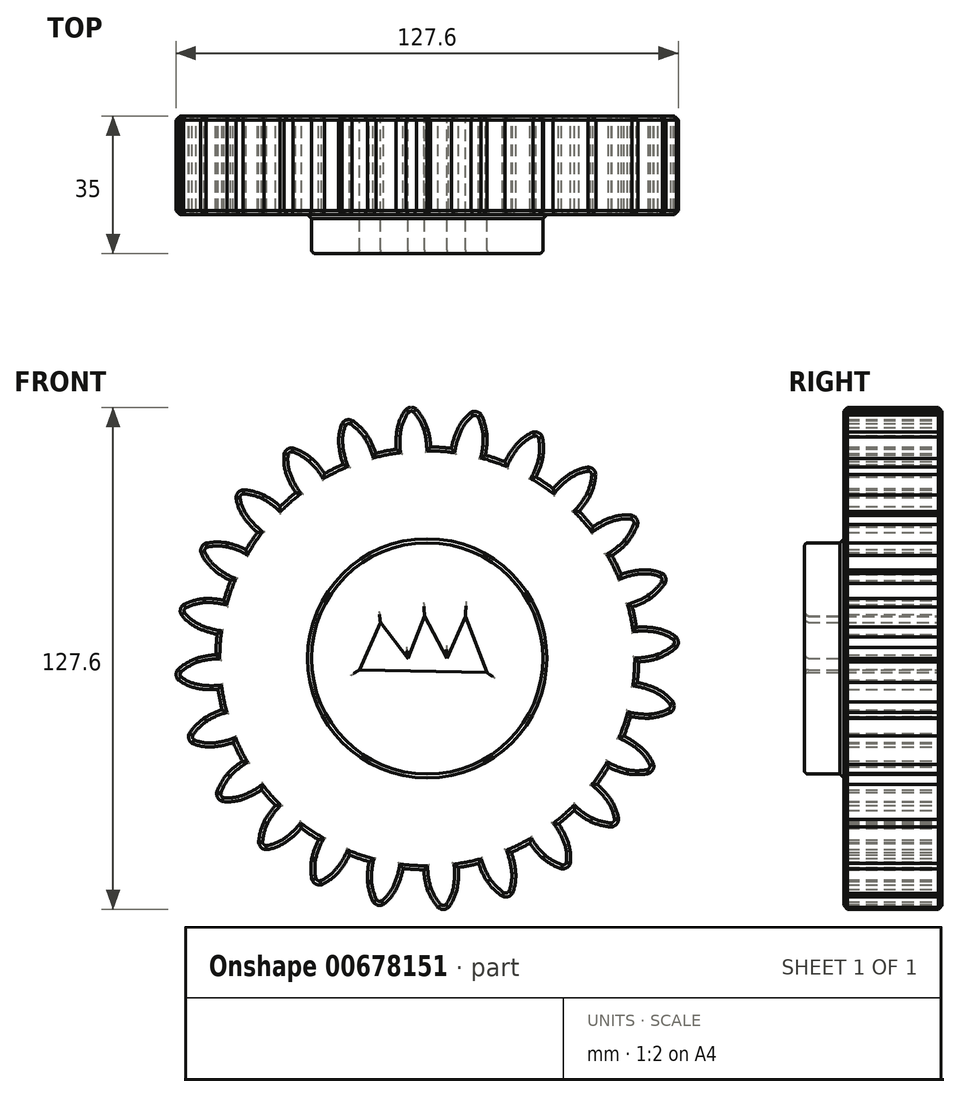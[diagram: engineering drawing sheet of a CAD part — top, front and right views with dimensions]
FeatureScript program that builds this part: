
annotation { "Feature Type Name" : "Feature", "Feature Type Description" : "" }
export const myFeature = defineFeature(function(context is Context, id is Id, definition is map)
    precondition{}
    {
        {
            var Q0;
            Q0=qCreatedBy(makeId("Front.planeOp"),FACE);
            var sketch = newSketch(context, id + "F0", { "sketchPlane" : qUnion([Q0])});
            skCircle(sketch, "E0", {"center": v(0, 0) * mm, "radius": 53.72 * mm});
            skCircle(sketch, "E1", {"center": v(0, 0) * mm, "radius": 58.67 * mm, "construction": true});
            skCircle(sketch, "E2", {"center": v(0, 0) * mm, "radius": 63.5 * mm, "construction": true});
            skLineSegment(sketch, "E3", {"start": v(0, 0) * mm, "end": v(0, 87.32) * mm, "construction": true});
            skLineSegment(sketch, "E4", {"start": v(0, 0) * mm, "end": v(-6.72, 102.52) * mm, "construction": true});
            skLineSegment(sketch, "E5", {"start": v(0, 58.67) * mm, "end": v(-57.61, 58.67) * mm, "construction": true});
            skLineSegment(sketch, "E6", {"start": v(0, 58.67) * mm, "end": v(-65.6, 34.8) * mm, "construction": true});
            skCircle(sketch, "E7", {"center": v(0, 0) * mm, "radius": 55.14 * mm, "construction": true});
            skCircle(sketch, "E8", {"center": v(0, 58.67) * mm, "radius": 14.6 * mm, "construction": true});
            skCircle(sketch, "E9", {"center": v(-13.72, 53.68) * mm, "radius": 14.6 * mm, "construction": true});
            skArc(sketch, "E10", {"start": v(0.88, 53.71) * mm, "mid": v(0.6, 56.22) * mm, "end": v(0, 58.67) * mm});
            skArc(sketch, "E11.MirrorCS", {"start": v(-7.66, 58.17) * mm, "mid": v(-6.86, 60.85) * mm, "end": v(-5.45, 63.27) * mm});
            skArc(sketch, "E12.MirrorCS", {"start": v(-7.88, 53.14) * mm, "mid": v(-7.93, 55.66) * mm, "end": v(-7.66, 58.17) * mm});
            skArc(sketch, "E13", {"start": v(0, 58.67) * mm, "mid": v(-1.18, 61.13) * mm, "end": v(-2.77, 63.34) * mm});
            skArc(sketch, "E14", {"start": v(-2.77, 63.34) * mm, "mid": v(-4.12, 63.8) * mm, "end": v(-5.45, 63.27) * mm});
            skCircle(sketch, "E15", {"center": v(0, 0) * mm, "radius": 29.38 * mm});
            skLineSegment(sketch, "E16", {"start": v(-17.22, -2.92) * mm, "end": v(-11.9, 9.15) * mm});
            skLineSegment(sketch, "E17", {"start": v(-11.9, 9.15) * mm, "end": v(-4.93, 0) * mm});
            skLineSegment(sketch, "E18", {"start": v(-4.93, 0) * mm, "end": v(-0.7, 10.8) * mm});
            skLineSegment(sketch, "E19", {"start": v(-0.7, 10.8) * mm, "end": v(5, 0) * mm});
            skLineSegment(sketch, "E20", {"start": v(5, 0) * mm, "end": v(9.74, 10.68) * mm});
            skLineSegment(sketch, "E21", {"start": v(9.74, 10.68) * mm, "end": v(15.18, -3.62) * mm});
            skLineSegment(sketch, "E22", {"start": v(15.18, -3.62) * mm, "end": v(-17.22, -2.92) * mm});
            skSolve(sketch);
        }
        {
            var Q0;
            {var subQ0=sQuery(id+"F0.wireOp",EDGE,"E0");var subQ1=makeQuery(id+"F0.imprint","INTERSECT",VERTEX,{"derivedFrom":[subQ0,sQuery(id+"F0.wireOp",EDGE,"E10")]});Q0=makeQuery(id+"F0.imprint","IMPRINT",FACE,{"disambiguationData":[TD([[makeQuery(id+"F0.imprint","IMPRINT",EDGE,{"disambiguationData":[TD([[subQ1,-1.0]])],"derivedFrom":subQ0}),1.0]])]});}
            var Q1;
            {var subQ1=sQuery(id+"F0.wireOp",EDGE,"E10");Q1=makeQuery(id+"F0.imprint","IMPRINT",FACE,{"disambiguationData":[TD([[makeQuery(id+"F0.imprint","IMPRINT",EDGE,{"derivedFrom":subQ1}),1.0]])]});}
            extrude(context, id + "F1", {"entities" : qUnion([Q0, Q1]), "depth" : 25 * mm, "offsetDistance" : 25 * mm});
        }
        {
            var Q0;
            Q0=makeQuery(id+"F1.opExtrude","SWEPT_BODY",BODY,{"disambiguationData":[OSD([sQuery(id+"F0.wireOp",EDGE,"E0"),sQuery(id+"F0.wireOp",EDGE,"E10"),sQuery(id+"F0.wireOp",EDGE,"E12.MirrorCS"),sQuery(id+"F0.wireOp",EDGE,"E11.MirrorCS"),sQuery(id+"F0.wireOp",EDGE,"E13"),sQuery(id+"F0.wireOp",EDGE,"E14")])]});
            var Q1;
            Q1=makeQuery(id+"F1.opExtrude","SWEPT_FACE",FACE,{"disambiguationData":[OSD([sQuery(id+"F0.wireOp",EDGE,"E0")])]});
            circularPattern(context, id + "F2", {"entities" : qUnion([Q0]), "axis" : qUnion([Q1]), "angle" : 360 * degree, "instanceCount" : 24, "equalSpace" : true});
        }
        {
            var Q0;
            Q0=makeQuery(id+"F0.imprint","IMPRINT",FACE,{"disambiguationData":[TD([[makeQuery(id+"F0.imprint","IMPRINT",EDGE,{"derivedFrom":sQuery(id+"F0.wireOp",EDGE,"E15")}),1.0]])]});
            extrude(context, id + "F3", {"entities" : qUnion([Q0]), "operationType" : NewBodyOperationType.ADD, "depth" : 35 * mm, "offsetDistance" : 25 * mm});
        }
        {
            var Q0;
            {var subQ0=makeQuery(id+"F1.opExtrude","CAP_FACE",FACE,{"disambiguationData":[OSD([sQuery(id+"F0.wireOp",EDGE,"E0"),sQuery(id+"F0.wireOp",EDGE,"E10"),sQuery(id+"F0.wireOp",EDGE,"E12.MirrorCS"),sQuery(id+"F0.wireOp",EDGE,"E11.MirrorCS"),sQuery(id+"F0.wireOp",EDGE,"E13"),sQuery(id+"F0.wireOp",EDGE,"E14"),sQuery(id+"F0.wireOp",EDGE,"E15")])],"isStart":false});Q0=makeQuery(id+"F3.boolean.opBoolean","MERGE",FACE,{"derivedFrom":[subQ0,makeQuery(id+"F2.opPattern","COPY",FACE,{"derivedFrom":subQ0,"instanceName":"1"}),makeQuery(id+"F2.opPattern","COPY",FACE,{"derivedFrom":subQ0,"instanceName":"2"}),makeQuery(id+"F2.opPattern","COPY",FACE,{"derivedFrom":subQ0,"instanceName":"3"}),makeQuery(id+"F2.opPattern","COPY",FACE,{"derivedFrom":subQ0,"instanceName":"4"}),makeQuery(id+"F2.opPattern","COPY",FACE,{"derivedFrom":subQ0,"instanceName":"5"}),makeQuery(id+"F2.opPattern","COPY",FACE,{"derivedFrom":subQ0,"instanceName":"6"}),makeQuery(id+"F2.opPattern","COPY",FACE,{"derivedFrom":subQ0,"instanceName":"7"}),makeQuery(id+"F2.opPattern","COPY",FACE,{"derivedFrom":subQ0,"instanceName":"8"}),makeQuery(id+"F2.opPattern","COPY",FACE,{"derivedFrom":subQ0,"instanceName":"9"}),makeQuery(id+"F2.opPattern","COPY",FACE,{"derivedFrom":subQ0,"instanceName":"10"}),makeQuery(id+"F2.opPattern","COPY",FACE,{"derivedFrom":subQ0,"instanceName":"11"}),makeQuery(id+"F2.opPattern","COPY",FACE,{"derivedFrom":subQ0,"instanceName":"12"}),makeQuery(id+"F2.opPattern","COPY",FACE,{"derivedFrom":subQ0,"instanceName":"13"}),makeQuery(id+"F2.opPattern","COPY",FACE,{"derivedFrom":subQ0,"instanceName":"14"}),makeQuery(id+"F2.opPattern","COPY",FACE,{"derivedFrom":subQ0,"instanceName":"15"}),makeQuery(id+"F2.opPattern","COPY",FACE,{"derivedFrom":subQ0,"instanceName":"16"}),makeQuery(id+"F2.opPattern","COPY",FACE,{"derivedFrom":subQ0,"instanceName":"17"}),makeQuery(id+"F2.opPattern","COPY",FACE,{"derivedFrom":subQ0,"instanceName":"18"}),makeQuery(id+"F2.opPattern","COPY",FACE,{"derivedFrom":subQ0,"instanceName":"19"}),makeQuery(id+"F2.opPattern","COPY",FACE,{"derivedFrom":subQ0,"instanceName":"20"}),makeQuery(id+"F2.opPattern","COPY",FACE,{"derivedFrom":subQ0,"instanceName":"21"}),makeQuery(id+"F2.opPattern","COPY",FACE,{"derivedFrom":subQ0,"instanceName":"22"}),makeQuery(id+"F2.opPattern","COPY",FACE,{"derivedFrom":subQ0,"instanceName":"23"})]});}
            chamfer(context, id + "F4", {"entities" : qUnion([Q0]), "width" : 1 * mm, "tangentPropagation" : true});
        }
        {
            var Q0;
            {var subQ0=sQuery(id+"F0.wireOp",EDGE,"E15");var subQ1=makeQuery(id+"F1.opExtrude","CAP_FACE",FACE,{"disambiguationData":[OSD([sQuery(id+"F0.wireOp",EDGE,"E0"),sQuery(id+"F0.wireOp",EDGE,"E10"),sQuery(id+"F0.wireOp",EDGE,"E12.MirrorCS"),sQuery(id+"F0.wireOp",EDGE,"E11.MirrorCS"),sQuery(id+"F0.wireOp",EDGE,"E13"),sQuery(id+"F0.wireOp",EDGE,"E14"),subQ0])],"isStart":true});Q0=makeQuery(id+"F3.boolean.opBoolean","MERGE",FACE,{"derivedFrom":[subQ1,makeQuery(id+"F2.opPattern","COPY",FACE,{"derivedFrom":subQ1,"instanceName":"1"}),makeQuery(id+"F2.opPattern","COPY",FACE,{"derivedFrom":subQ1,"instanceName":"2"}),makeQuery(id+"F2.opPattern","COPY",FACE,{"derivedFrom":subQ1,"instanceName":"3"}),makeQuery(id+"F2.opPattern","COPY",FACE,{"derivedFrom":subQ1,"instanceName":"4"}),makeQuery(id+"F2.opPattern","COPY",FACE,{"derivedFrom":subQ1,"instanceName":"5"}),makeQuery(id+"F2.opPattern","COPY",FACE,{"derivedFrom":subQ1,"instanceName":"6"}),makeQuery(id+"F2.opPattern","COPY",FACE,{"derivedFrom":subQ1,"instanceName":"7"}),makeQuery(id+"F2.opPattern","COPY",FACE,{"derivedFrom":subQ1,"instanceName":"8"}),makeQuery(id+"F2.opPattern","COPY",FACE,{"derivedFrom":subQ1,"instanceName":"9"}),makeQuery(id+"F2.opPattern","COPY",FACE,{"derivedFrom":subQ1,"instanceName":"10"}),makeQuery(id+"F2.opPattern","COPY",FACE,{"derivedFrom":subQ1,"instanceName":"11"}),makeQuery(id+"F2.opPattern","COPY",FACE,{"derivedFrom":subQ1,"instanceName":"12"}),makeQuery(id+"F2.opPattern","COPY",FACE,{"derivedFrom":subQ1,"instanceName":"13"}),makeQuery(id+"F2.opPattern","COPY",FACE,{"derivedFrom":subQ1,"instanceName":"14"}),makeQuery(id+"F2.opPattern","COPY",FACE,{"derivedFrom":subQ1,"instanceName":"15"}),makeQuery(id+"F2.opPattern","COPY",FACE,{"derivedFrom":subQ1,"instanceName":"16"}),makeQuery(id+"F2.opPattern","COPY",FACE,{"derivedFrom":subQ1,"instanceName":"17"}),makeQuery(id+"F2.opPattern","COPY",FACE,{"derivedFrom":subQ1,"instanceName":"18"}),makeQuery(id+"F2.opPattern","COPY",FACE,{"derivedFrom":subQ1,"instanceName":"19"}),makeQuery(id+"F2.opPattern","COPY",FACE,{"derivedFrom":subQ1,"instanceName":"20"}),makeQuery(id+"F2.opPattern","COPY",FACE,{"derivedFrom":subQ1,"instanceName":"21"}),makeQuery(id+"F2.opPattern","COPY",FACE,{"derivedFrom":subQ1,"instanceName":"22"}),makeQuery(id+"F2.opPattern","COPY",FACE,{"derivedFrom":subQ1,"instanceName":"23"}),makeQuery(id+"F3.opExtrude","CAP_FACE",FACE,{"disambiguationData":[OSD([subQ0,sQuery(id+"F0.wireOp",EDGE,"JNtdXsKn-sl94-sJaL-X6j9-ipqJ5UrsfOhM"),sQuery(id+"F0.wireOp",EDGE,"nhLlYziE-T9go-qMXb-Lngr-M2SgK2O0rp0T"),sQuery(id+"F0.wireOp",EDGE,"FmWoKXcW-Qzj9-4IRf-52Ky-pHPL5FFvMOR0"),sQuery(id+"F0.wireOp",EDGE,"DI1x3HvC-3bFb-MIyR-UmgX-l09uo7GKVcLs"),sQuery(id+"F0.wireOp",EDGE,"HNXKMdma-7YMK-hGZH-avgI-vMgkNqy3HRcJ"),sQuery(id+"F0.wireOp",EDGE,"5TuZqJqq-FCUH-1mfl-Rlqv-17RgC5mEEKbx"),sQuery(id+"F0.wireOp",EDGE,"hMIrZLfI-JfvP-B32Z-qgZj-gbDX4PTdaB8e")])],"isStart":true})]});}
            chamfer(context, id + "F5", {"entities" : qUnion([Q0]), "width" : mm, "tangentPropagation" : true});
        }
        {
            var Q0;
            Q0=makeQuery(id+"F3.opExtrude","CAP_FACE",FACE,{"disambiguationData":[OSD([sQuery(id+"F0.wireOp",EDGE,"E15"),sQuery(id+"F0.wireOp",EDGE,"JNtdXsKn-sl94-sJaL-X6j9-ipqJ5UrsfOhM"),sQuery(id+"F0.wireOp",EDGE,"nhLlYziE-T9go-qMXb-Lngr-M2SgK2O0rp0T"),sQuery(id+"F0.wireOp",EDGE,"FmWoKXcW-Qzj9-4IRf-52Ky-pHPL5FFvMOR0"),sQuery(id+"F0.wireOp",EDGE,"DI1x3HvC-3bFb-MIyR-UmgX-l09uo7GKVcLs"),sQuery(id+"F0.wireOp",EDGE,"HNXKMdma-7YMK-hGZH-avgI-vMgkNqy3HRcJ"),sQuery(id+"F0.wireOp",EDGE,"5TuZqJqq-FCUH-1mfl-Rlqv-17RgC5mEEKbx"),sQuery(id+"F0.wireOp",EDGE,"hMIrZLfI-JfvP-B32Z-qgZj-gbDX4PTdaB8e")])],"isStart":false});
            fillet(context, id + "F6", {"entities" : qUnion([Q0]), "radius" : 1 * mm, "tangentPropagation" : true, "allowEdgeOverflow" : false});
        }
        {
            var Q0;
            {var subQ0=sQuery(id+"F0.wireOp",EDGE,"E15");var subQ1=makeQuery(id+"F1.opExtrude","CAP_FACE",FACE,{"disambiguationData":[OSD([sQuery(id+"F0.wireOp",EDGE,"E0"),sQuery(id+"F0.wireOp",EDGE,"E10"),sQuery(id+"F0.wireOp",EDGE,"E12.MirrorCS"),sQuery(id+"F0.wireOp",EDGE,"E11.MirrorCS"),sQuery(id+"F0.wireOp",EDGE,"E13"),sQuery(id+"F0.wireOp",EDGE,"E14"),subQ0])],"isStart":true});Q0=makeQuery(id+"F3.boolean.opBoolean","MERGE",FACE,{"derivedFrom":[subQ1,makeQuery(id+"F2.opPattern","COPY",FACE,{"derivedFrom":subQ1,"instanceName":"1"}),makeQuery(id+"F2.opPattern","COPY",FACE,{"derivedFrom":subQ1,"instanceName":"2"}),makeQuery(id+"F2.opPattern","COPY",FACE,{"derivedFrom":subQ1,"instanceName":"3"}),makeQuery(id+"F2.opPattern","COPY",FACE,{"derivedFrom":subQ1,"instanceName":"4"}),makeQuery(id+"F2.opPattern","COPY",FACE,{"derivedFrom":subQ1,"instanceName":"5"}),makeQuery(id+"F2.opPattern","COPY",FACE,{"derivedFrom":subQ1,"instanceName":"6"}),makeQuery(id+"F2.opPattern","COPY",FACE,{"derivedFrom":subQ1,"instanceName":"7"}),makeQuery(id+"F2.opPattern","COPY",FACE,{"derivedFrom":subQ1,"instanceName":"8"}),makeQuery(id+"F2.opPattern","COPY",FACE,{"derivedFrom":subQ1,"instanceName":"9"}),makeQuery(id+"F2.opPattern","COPY",FACE,{"derivedFrom":subQ1,"instanceName":"10"}),makeQuery(id+"F2.opPattern","COPY",FACE,{"derivedFrom":subQ1,"instanceName":"11"}),makeQuery(id+"F2.opPattern","COPY",FACE,{"derivedFrom":subQ1,"instanceName":"12"}),makeQuery(id+"F2.opPattern","COPY",FACE,{"derivedFrom":subQ1,"instanceName":"13"}),makeQuery(id+"F2.opPattern","COPY",FACE,{"derivedFrom":subQ1,"instanceName":"14"}),makeQuery(id+"F2.opPattern","COPY",FACE,{"derivedFrom":subQ1,"instanceName":"15"}),makeQuery(id+"F2.opPattern","COPY",FACE,{"derivedFrom":subQ1,"instanceName":"16"}),makeQuery(id+"F2.opPattern","COPY",FACE,{"derivedFrom":subQ1,"instanceName":"17"}),makeQuery(id+"F2.opPattern","COPY",FACE,{"derivedFrom":subQ1,"instanceName":"18"}),makeQuery(id+"F2.opPattern","COPY",FACE,{"derivedFrom":subQ1,"instanceName":"19"}),makeQuery(id+"F2.opPattern","COPY",FACE,{"derivedFrom":subQ1,"instanceName":"20"}),makeQuery(id+"F2.opPattern","COPY",FACE,{"derivedFrom":subQ1,"instanceName":"21"}),makeQuery(id+"F2.opPattern","COPY",FACE,{"derivedFrom":subQ1,"instanceName":"22"}),makeQuery(id+"F2.opPattern","COPY",FACE,{"derivedFrom":subQ1,"instanceName":"23"}),makeQuery(id+"F3.opExtrude","CAP_FACE",FACE,{"disambiguationData":[OSD([subQ0,sQuery(id+"F0.wireOp",EDGE,"JNtdXsKn-sl94-sJaL-X6j9-ipqJ5UrsfOhM"),sQuery(id+"F0.wireOp",EDGE,"nhLlYziE-T9go-qMXb-Lngr-M2SgK2O0rp0T"),sQuery(id+"F0.wireOp",EDGE,"FmWoKXcW-Qzj9-4IRf-52Ky-pHPL5FFvMOR0"),sQuery(id+"F0.wireOp",EDGE,"DI1x3HvC-3bFb-MIyR-UmgX-l09uo7GKVcLs"),sQuery(id+"F0.wireOp",EDGE,"HNXKMdma-7YMK-hGZH-avgI-vMgkNqy3HRcJ"),sQuery(id+"F0.wireOp",EDGE,"5TuZqJqq-FCUH-1mfl-Rlqv-17RgC5mEEKbx"),sQuery(id+"F0.wireOp",EDGE,"hMIrZLfI-JfvP-B32Z-qgZj-gbDX4PTdaB8e")])],"isStart":true})]});}
            fillet(context, id + "F7", {"entities" : qUnion([Q0]), "radius" : 1 * mm, "tangentPropagation" : true, "allowEdgeOverflow" : false});
        }
    });
